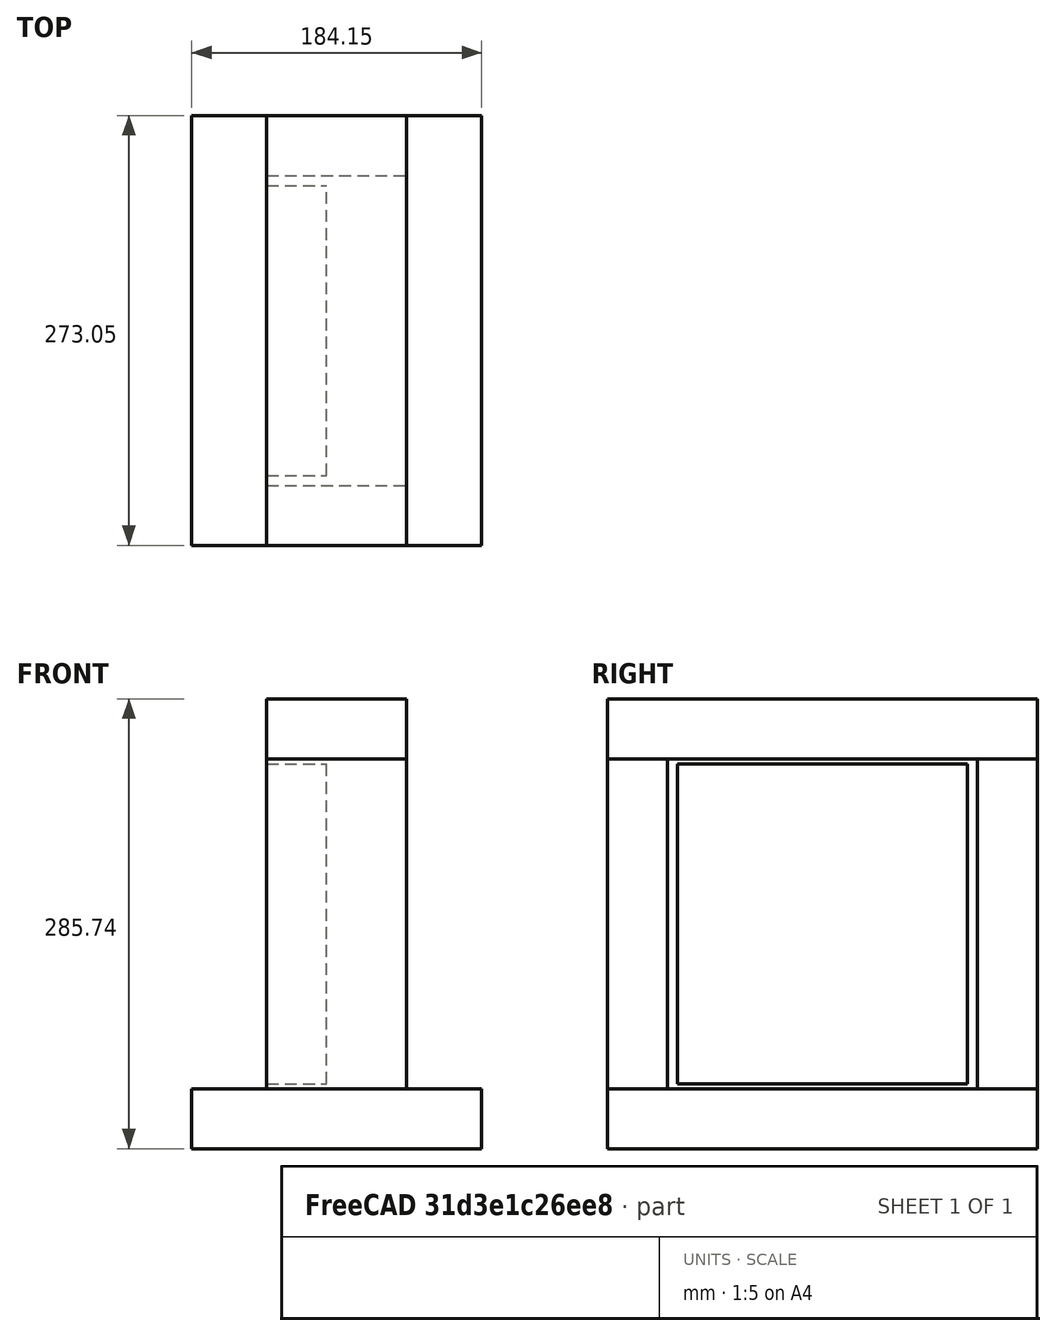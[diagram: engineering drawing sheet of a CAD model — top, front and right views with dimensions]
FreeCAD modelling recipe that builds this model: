
FCSTD DOCUMENT  (FreeCAD 0.19R24291 (Git))
Label: Door Mockup
License: All rights reserved
LicenseURL: http://en.wikipedia.org/wiki/All_rights_reserved
objects: Part::Box×5, Spreadsheet::Sheet×2
note: 5 computed .brp shape members not serialized (recipe doc carries the construction recipe); baked Part::Feature solids carry a one-line shape summary decoded from their .brp

FEATURE [Part::Box] Box  label="Door"
  AttacherType = Attacher::AttachEngine3D
  Height = 203.2
  Length = 38.1
  Width = 184.15
  expr: Height = Spreadsheet.DoorHeight
  expr: Width = Spreadsheet.DoorWidth
  expr: Length = Spreadsheet.two
FEATURE [Spreadsheet::Sheet] Spreadsheet  label="Dimensions"
  cells = A1=Door Height; B1(DoorHeight)==8in; A2=Door Width; B2(DoorWidth)==B7; A3=Door Height Gap; B3(DoorHGap)==0.25in; A4=Door Width Gap; B4(DoorWGap)==0.5in; A5=2 in nominal; B5(two)==1.5in; A6=4 in nominal; B6(four)==3.5in; A7=8 in nominal; B7(eight)==7.25in; H18=0
FEATURE [Part::Box] Box001  label="Baseplate"
  AttacherType = Attacher::AttachEngine3D
  Height = 38.1
  Length = 184.15
  Placement = pos=(-47.625,-44.45,-41.275) rot=(0,0,1;0rad)
  Width = 273.05
  expr: Length = Spreadsheet.eight
  expr: .Placement.Base.x = -Spreadsheet.eight / 2 + Spreadsheet.four / 2
  expr: Height = Spreadsheet.two
  expr: .Placement.Base.z = -Spreadsheet.two - Spreadsheet.DoorHGap / 2
  expr: Width = Spreadsheet.DoorWidth + Spreadsheet.DoorWGap + Spreadsheet.two * 2
  expr: .Placement.Base.y = -Spreadsheet.DoorWGap / 2 - Spreadsheet.two
FEATURE [Part::Box] Box002  label="RUpright"
  AttacherType = Attacher::AttachEngine3D
  Height = 209.55
  Length = 88.9
  Placement = pos=(0,-44.45,-3.175) rot=(0,0,1;0rad)
  Width = 38.1
  expr: .Placement.Base.y = -Spreadsheet.DoorWGap / 2 - Spreadsheet.two
  expr: Width = Spreadsheet.two
  expr: .Placement.Base.z = -Spreadsheet.DoorHGap / 2
  expr: Height = Spreadsheet.DoorHeight + Spreadsheet.DoorHGap
  expr: Length = Spreadsheet.four
FEATURE [Part::Box] Box003  label="LUpright"
  AttacherType = Attacher::AttachEngine3D
  Height = 209.55
  Length = 88.9
  Placement = pos=(0,190.5,-3.175) rot=(0,0,1;0rad)
  Width = 38.1
  expr: Length = Spreadsheet.four
  expr: Height = Spreadsheet.DoorHeight + Spreadsheet.DoorHGap
  expr: .Placement.Base.z = -Spreadsheet.DoorHGap / 2
  expr: Width = Spreadsheet.two
  expr: .Placement.Base.y = Spreadsheet.DoorWidth + Spreadsheet.DoorWGap / 2
FEATURE [Part::Box] Box004  label="Lintel"
  AttacherType = Attacher::AttachEngine3D
  Height = 38.1
  Length = 88.9
  Placement = pos=(0,-44.45,206.375) rot=(0,0,1;0rad)
  Width = 273.05
  expr: .Placement.Base.z = Spreadsheet.DoorHeight + Spreadsheet.DoorHGap / 2
  expr: .Placement.Base.y = -Spreadsheet.DoorWGap / 2 - Spreadsheet.two
  expr: Width = Spreadsheet.DoorWidth + Spreadsheet.DoorWGap + Spreadsheet.two * 2
  expr: Height = Spreadsheet.two
  expr: Length = Spreadsheet.four
FEATURE [Spreadsheet::Sheet] Spreadsheet001  label="Cut Lengths"
  cells = B1=2x8; A2=Door; B2==<<Door>>.Height; A3=Baseplate; B3==<<Baseplate>>.Width; B4=2x4; A5=Lintel; B5==<<Lintel>>.Width; A6=Left Upright; B6==<<LUpright>>.Height; A7=Right Upright; B7==<<RUpright>>.Height
